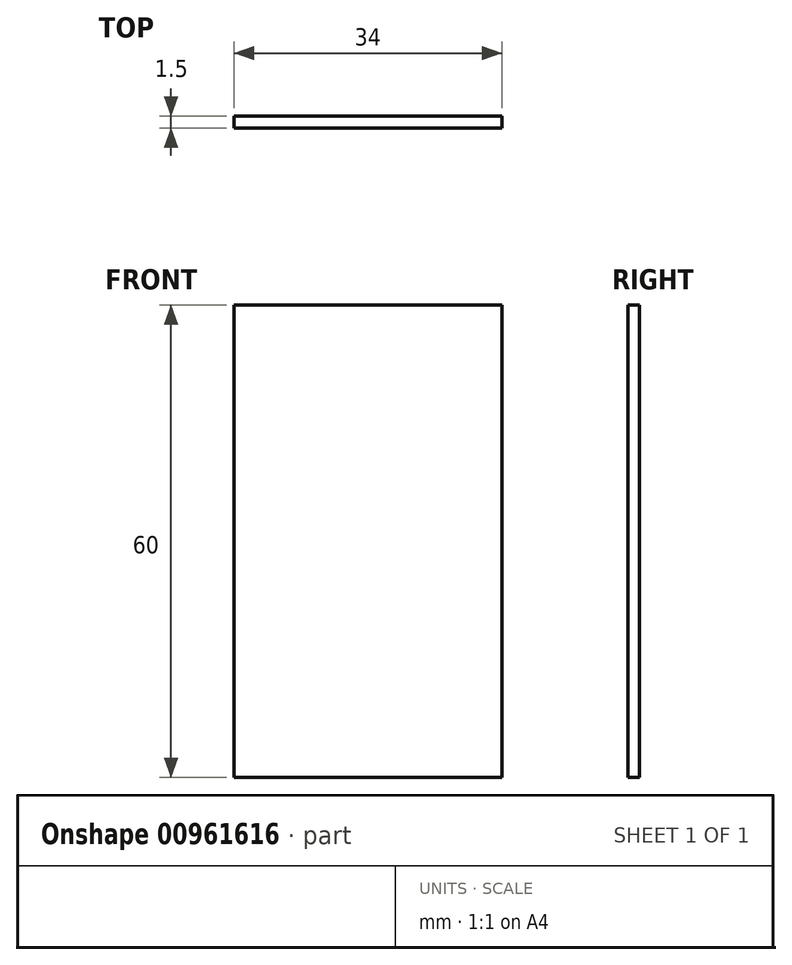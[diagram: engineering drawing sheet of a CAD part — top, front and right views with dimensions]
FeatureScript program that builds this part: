
annotation { "Feature Type Name" : "Feature", "Feature Type Description" : "" }
export const myFeature = defineFeature(function(context is Context, id is Id, definition is map)
    precondition{}
    {
        {
            var Q0;
            Q0=qCreatedBy(makeId("Front.planeOp"),FACE);
            var sketch = newSketch(context, id + "F0", { "sketchPlane" : qUnion([Q0])});
            skLineSegment(sketch, "E0.bottom", {"start": v(-17, 30) * mm, "end": v(17, 30) * mm});
            skLineSegment(sketch, "E0.top", {"start": v(-17, -30) * mm, "end": v(17, -30) * mm});
            skLineSegment(sketch, "E0.left", {"start": v(-17, 30) * mm, "end": v(-17, -30) * mm});
            skLineSegment(sketch, "E0.right", {"start": v(17, 30) * mm, "end": v(17, -30) * mm});
            skPoint(sketch, "E0.middle", {"position": v(0, 0) * mm});
            skSolve(sketch);
        }
        {
            var Q0;
            Q0=makeQuery(id+"F0.imprint","IMPRINT",FACE,{"disambiguationData":[TD([[makeQuery(id+"F0.imprint","IMPRINT",EDGE,{"derivedFrom":sQuery(id+"F0.wireOp",EDGE,"E0.bottom")}),-1.0]])]});
            extrude(context, id + "F1", {"entities" : qUnion([Q0]), "depth" : 1.5 * mm, "offsetDistance" : 25 * mm});
        }
        {
            var Q0;
            Q0=makeQuery(id+"F1.opExtrude","SWEPT_BODY",BODY,{"disambiguationData":[OSD([sQuery(id+"F0.wireOp",EDGE,"E0.bottom"),sQuery(id+"F0.wireOp",EDGE,"E0.top"),sQuery(id+"F0.wireOp",EDGE,"E0.left"),sQuery(id+"F0.wireOp",EDGE,"E0.right")])]});
            transform(context, id + "F2", {"entities" : qUnion([Q0]), "transformType" : TransformType.TRANSLATION_3D, "dx" : 0 * mm, "dy" : 0.5 * mm, "dz" : 0 * mm, "makeCopy" : false});
        }
    });
